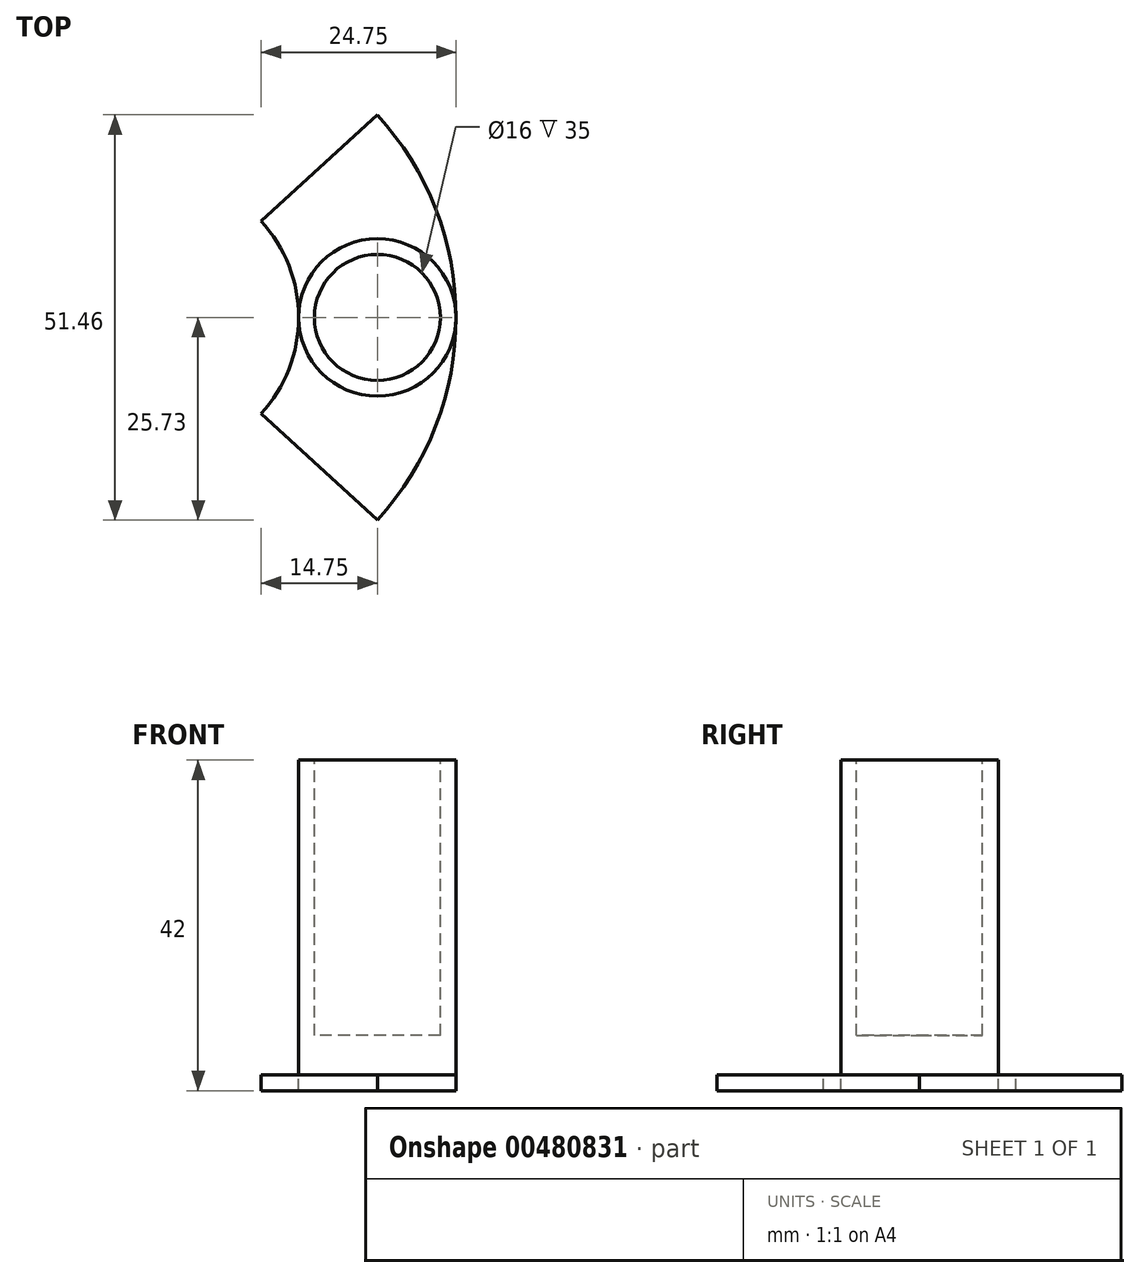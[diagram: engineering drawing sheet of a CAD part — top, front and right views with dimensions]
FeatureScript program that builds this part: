
annotation { "Feature Type Name" : "Feature", "Feature Type Description" : "" }
export const myFeature = defineFeature(function(context is Context, id is Id, definition is map)
    precondition{}
    {
        {
            var Q0;
            Q0=qCreatedBy(makeId("Top.planeOp"),FACE);
            var sketch = newSketch(context, id + "F0", { "sketchPlane" : qUnion([Q0])});
            skCircle(sketch, "E0", {"center": v(0, 0) * mm, "radius": 10 * mm});
            skSolve(sketch);
        }
        {
            var Q0;
            Q0 = qSketchRegion(id + "F0", true);
            extrude(context, id + "F1", {"entities" : qUnion([Q0]), "depth" : 40 * mm});
        }
        {
            var Q0;
            Q0=makeQuery(id+"F1.opExtrude","CAP_FACE",FACE,{"disambiguationData":[OSD([sQuery(id+"F0.wireOp",EDGE,"E0")])],"isStart":false});
            var sketch = newSketch(context, id + "F2", { "sketchPlane" : qUnion([Q0])});
            skCircle(sketch, "E1", {"center": v(0, 0) * mm, "radius": 8 * mm});
            skSolve(sketch);
        }
        {
            var Q0;
            Q0 = qSketchRegion(id + "F2", true);
            extrude(context, id + "F3", {"entities" : qUnion([Q0]), "operationType" : NewBodyOperationType.REMOVE, "oppositeDirection" : true, "depth" : 35 * mm});
        }
        {
            var Q0;
            Q0=makeQuery(id+"F1.opExtrude","CAP_FACE",FACE,{"disambiguationData":[OSD([sQuery(id+"F0.wireOp",EDGE,"E0")])],"isStart":true});
            var sketch = newSketch(context, id + "F4", { "sketchPlane" : qUnion([Q0])});
            skLineSegment(sketch, "E2", {"start": v(0, 0) * mm, "end": v(10, 0) * mm});
            skLineSegment(sketch, "E3", {"start": v(10, 0) * mm, "end": v(-28.1, 0) * mm});
            skCircle(sketch, "E4", {"center": v(-28.1, 0) * mm, "radius": 38.1 * mm});
            skCircle(sketch, "E5.0", {"center": v(-28.1, 0) * mm, "radius": 18.1 * mm});
            skLineSegment(sketch, "E6", {"start": v(-28.1, 0) * mm, "end": v(0, 25.73) * mm});
            skLineSegment(sketch, "E7.MirrorCS", {"start": v(-28.1, 0) * mm, "end": v(0, -25.73) * mm});
            skLineSegment(sketch, "E8", {"start": v(-28.1, 0) * mm, "end": v(-10, 0) * mm});
            skSolve(sketch);
        }
        {
            var Q0;
            {var subQ0=sQuery(id+"F4.wireOp",EDGE,"E3");var subQ3=makeQuery(id+"F4.imprint","IMPRINT",VERTEX,{"derivedFrom":subQ0});Q0=makeQuery(id+"F4.imprint","IMPRINT",FACE,{"disambiguationData":[TD([[makeQuery(id+"F4.imprint","IMPRINT",EDGE,{"disambiguationData":[TD([[subQ3,-1.0]])],"derivedFrom":subQ0}),-1.0]])]});}
            var Q1;
            {var subQ0=sQuery(id+"F4.wireOp",EDGE,"E3");var subQ3=makeQuery(id+"F4.imprint","IMPRINT",VERTEX,{"derivedFrom":subQ0});Q1=makeQuery(id+"F4.imprint","IMPRINT",FACE,{"disambiguationData":[TD([[makeQuery(id+"F4.imprint","IMPRINT",EDGE,{"disambiguationData":[TD([[subQ3,-1.0]])],"derivedFrom":subQ0}),1.0]])]});}
            var Q2;
            {var subQ3=sQuery(id+"F4.wireOp",EDGE,"E6");var subQ5=sQuery(id+"F4.wireOp",EDGE,"E5.0");var subQ6=makeQuery(id+"F4.imprint","INTERSECT",VERTEX,{"derivedFrom":[subQ5,subQ3]});Q2=makeQuery(id+"F4.imprint","IMPRINT",FACE,{"disambiguationData":[TD([[makeQuery(id+"F4.imprint","IMPRINT",EDGE,{"disambiguationData":[TD([[subQ6,1.0]])],"derivedFrom":subQ5}),-1.0]])]});}
            var Q3;
            {var subQ3=sQuery(id+"F4.wireOp",EDGE,"E7.MirrorCS");var subQ5=sQuery(id+"F4.wireOp",EDGE,"E5.0");var subQ6=makeQuery(id+"F4.imprint","INTERSECT",VERTEX,{"derivedFrom":[subQ5,subQ3]});Q3=makeQuery(id+"F4.imprint","IMPRINT",FACE,{"disambiguationData":[TD([[makeQuery(id+"F4.imprint","IMPRINT",EDGE,{"disambiguationData":[TD([[subQ6,-1.0]])],"derivedFrom":subQ5}),-1.0]])]});}
            extrude(context, id + "F5", {"entities" : qUnion([Q0, Q1, Q2, Q3]), "operationType" : NewBodyOperationType.ADD, "depth" : 2 * mm});
        }
    });
